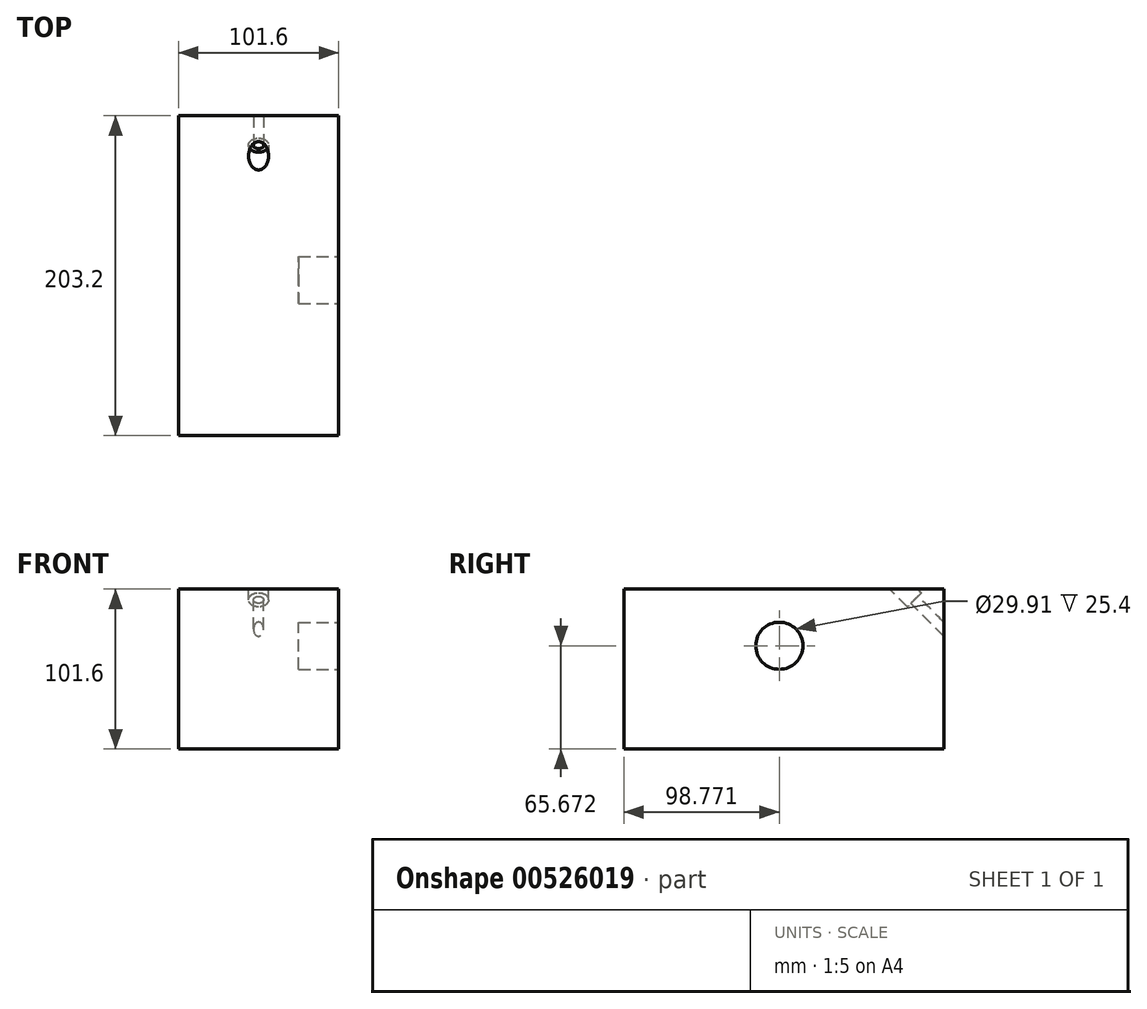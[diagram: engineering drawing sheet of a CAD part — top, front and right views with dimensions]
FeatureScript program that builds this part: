
annotation { "Feature Type Name" : "Feature", "Feature Type Description" : "" }
export const myFeature = defineFeature(function(context is Context, id is Id, definition is map)
    precondition{}
    {
        {
            var Q0;
            Q0=qCreatedBy(makeId("Front.planeOp"),FACE);
            var sketch = newSketch(context, id + "F0", { "sketchPlane" : qUnion([Q0])});
            skLineSegment(sketch, "E0.bottom", {"start": v(0, 0) * mm, "end": v(101.6, 0) * mm});
            skLineSegment(sketch, "E0.top", {"start": v(0, 101.6) * mm, "end": v(101.6, 101.6) * mm});
            skLineSegment(sketch, "E0.left", {"start": v(0, 0) * mm, "end": v(0, 101.6) * mm});
            skLineSegment(sketch, "E0.right", {"start": v(101.6, 0) * mm, "end": v(101.6, 101.6) * mm});
            skSolve(sketch);
        }
        {
            var Q0;
            Q0 = qSketchRegion(id + "F0", true);
            extrude(context, id + "F1", {"entities" : qUnion([Q0]), "depth" : 203.2 * mm, "offsetDistance" : 25.4 * mm});
        }
        {
            var Q0;
            Q0=makeQuery(id+"F1.opExtrude","SWEPT_FACE",FACE,{"disambiguationData":[OSD([sQuery(id+"F0.wireOp",EDGE,"E0.top")])]});
            var sketch = newSketch(context, id + "F2", { "sketchPlane" : qUnion([Q0])});
            skLineSegment(sketch, "E1", {"start": v(0, -25.4) * mm, "end": v(101.6, -25.4) * mm, "construction": true});
            skSolve(sketch);
        }
        {
            var Q0;
            Q0=sQuery(id+"F2.wireOp",EDGE,"E1");
            cPlane(context, id + "F3", {"entities" : qUnion([Q0]), "cplaneType" : CPlaneType.LINE_ANGLE, "offset" : 25.4 * mm, "angle" : 45 * degree, "oppositeDirection" : true, "width" : 152.4 * mm, "height" : 152.4 * mm});
        }
        {
            var Q0;
            Q0=qCreatedBy(id+"F3.planeOp",FACE);
            var sketch = newSketch(context, id + "F4", { "sketchPlane" : qUnion([Q0])});
            skLineSegment(sketch, "E2.0", {"start": v(0, 53.88) * mm, "end": v(-101.6, 53.88) * mm, "construction": true});
            skCircle(sketch, "E3", {"center": v(-50.8, 53.88) * mm, "radius": 3.18 * mm});
            skCircle(sketch, "E4", {"center": v(-50.8, 53.88) * mm, "radius": 6.35 * mm});
            skSolve(sketch);
        }
        {
            var Q0;
            Q0=makeQuery(id+"F4.imprint","IMPRINT",FACE,{"disambiguationData":[TD([[makeQuery(id+"F4.imprint","IMPRINT",EDGE,{"derivedFrom":sQuery(id+"F4.wireOp",EDGE,"E3")}),1.0]])]});
            extrude(context, id + "F5", {"entities" : qUnion([Q0]), "operationType" : NewBodyOperationType.REMOVE, "endBound" : BoundingType.THROUGH_ALL, "depth" : 25.4 * mm, "offsetDistance" : 25.4 * mm});
        }
        {
            var Q0;
            Q0=makeQuery(id+"F4.imprint","IMPRINT",FACE,{"disambiguationData":[TD([[makeQuery(id+"F4.imprint","IMPRINT",EDGE,{"derivedFrom":sQuery(id+"F4.wireOp",EDGE,"E3")}),1.0]])]});
            var Q1;
            Q1=makeQuery(id+"F4.imprint","IMPRINT",FACE,{"disambiguationData":[TD([[makeQuery(id+"F4.imprint","IMPRINT",EDGE,{"derivedFrom":sQuery(id+"F4.wireOp",EDGE,"E3")}),-1.0]])]});
            extrude(context, id + "F6", {"entities" : qUnion([Q0, Q1]), "operationType" : NewBodyOperationType.REMOVE, "depth" : 9.52 * mm, "offsetDistance" : 25.4 * mm, "hasSecondDirection" : true, "secondDirectionBound" : BoundingType.THROUGH_ALL, "secondDirectionOppositeDirection" : true, "secondDirectionDepth" : 25.4 * mm});
        }
        {
            var Q0;
            {var subQ0=sQuery(id+"F0.wireOp",EDGE,"E0.top");Q0=makeQuery(id+"F2.imprint","IMPRINT",FACE,{"disambiguationData":[TD([[makeQuery(id+"F2.imprint","IMPRINT",EDGE,{"derivedFrom":makeQuery(id+"F1.opExtrude","CAP_EDGE",EDGE,{"disambiguationData":[OSD([subQ0])],"isStart":true})}),-1.0]])]});}
            var Q1;
            Q1=makeQuery(id+"F1.opExtrude","SWEPT_FACE",FACE,{"disambiguationData":[OSD([sQuery(id+"F0.wireOp",EDGE,"E0.bottom")])]});
            cPlane(context, id + "F7", {"entities" : qUnion([Q0, Q1]), "cplaneType" : CPlaneType.MID_PLANE, "offset" : 25.4 * mm, "width" : 152.4 * mm, "height" : 152.4 * mm});
        }
        {
            var Q0;
            Q0=makeQuery(id+"F1.opExtrude","SWEPT_FACE",FACE,{"disambiguationData":[OSD([sQuery(id+"F0.wireOp",EDGE,"E0.right")])]});
            var sketch = newSketch(context, id + "F8", { "sketchPlane" : qUnion([Q0])});
            skCircle(sketch, "E5", {"center": v(-104.43, 65.67) * mm, "radius": 14.96 * mm});
            skSolve(sketch);
        }
        {
            var Q0;
            Q0=makeQuery(id+"F8.imprint","IMPRINT",FACE,{"disambiguationData":[TD([[makeQuery(id+"F8.imprint","IMPRINT",EDGE,{"derivedFrom":sQuery(id+"F8.wireOp",EDGE,"E5")}),1.0]])]});
            extrude(context, id + "F9", {"entities" : qUnion([Q0]), "operationType" : NewBodyOperationType.REMOVE, "oppositeDirection" : true, "depth" : 25.4 * mm, "offsetDistance" : 25.4 * mm});
        }
    });
